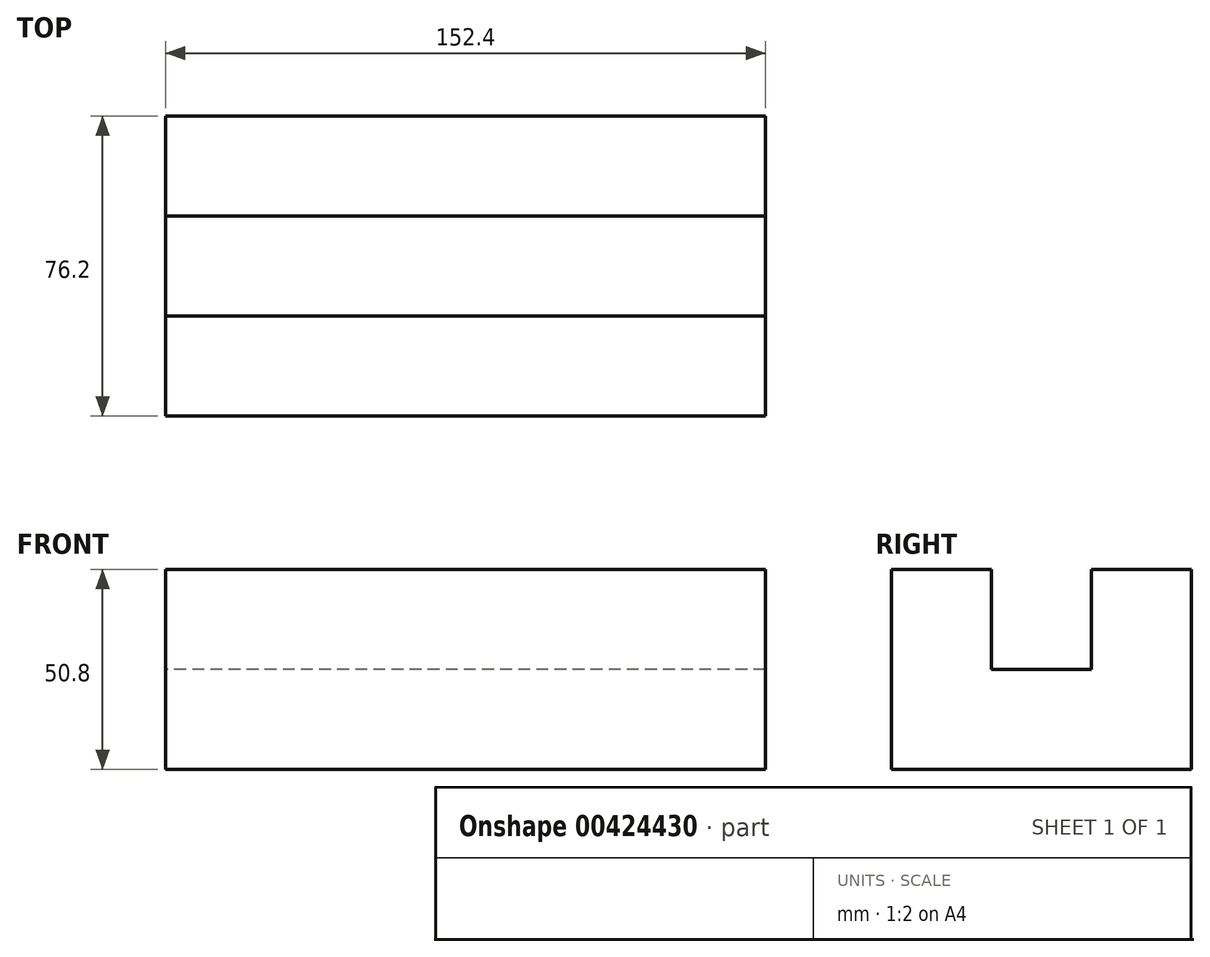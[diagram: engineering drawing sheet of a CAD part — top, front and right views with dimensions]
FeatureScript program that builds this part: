
annotation { "Feature Type Name" : "Feature", "Feature Type Description" : "" }
export const myFeature = defineFeature(function(context is Context, id is Id, definition is map)
    precondition{}
    {
        {
            var Q0;
            Q0=qCreatedBy(makeId("Right.planeOp"),FACE);
            var sketch = newSketch(context, id + "F0", { "sketchPlane" : qUnion([Q0])});
            skLineSegment(sketch, "E0", {"start": v(0, 0) * mm, "end": v(-76.2, 0) * mm});
            skLineSegment(sketch, "E1", {"start": v(-76.2, 0) * mm, "end": v(-76.2, 50.8) * mm});
            skLineSegment(sketch, "E2", {"start": v(-76.2, 50.8) * mm, "end": v(-50.8, 50.8) * mm});
            skLineSegment(sketch, "E3", {"start": v(-50.8, 50.8) * mm, "end": v(-50.8, 25.4) * mm});
            skLineSegment(sketch, "E4", {"start": v(-50.8, 25.4) * mm, "end": v(-25.4, 25.4) * mm});
            skLineSegment(sketch, "E5", {"start": v(-25.4, 25.4) * mm, "end": v(-25.4, 50.8) * mm});
            skLineSegment(sketch, "E6", {"start": v(-25.4, 50.8) * mm, "end": v(0, 50.8) * mm});
            skLineSegment(sketch, "E7", {"start": v(0, 50.8) * mm, "end": v(0, 0) * mm});
            skSolve(sketch);
        }
        {
            var Q0;
            Q0=makeQuery(id+"F0.imprint","IMPRINT",FACE,{"disambiguationData":[TD([[makeQuery(id+"F0.imprint","IMPRINT",EDGE,{"derivedFrom":sQuery(id+"F0.wireOp",EDGE,"E0")}),-1.0]])]});
            extrude(context, id + "F1", {"entities" : qUnion([Q0]), "depth" : 152.4 * mm});
        }
    });
